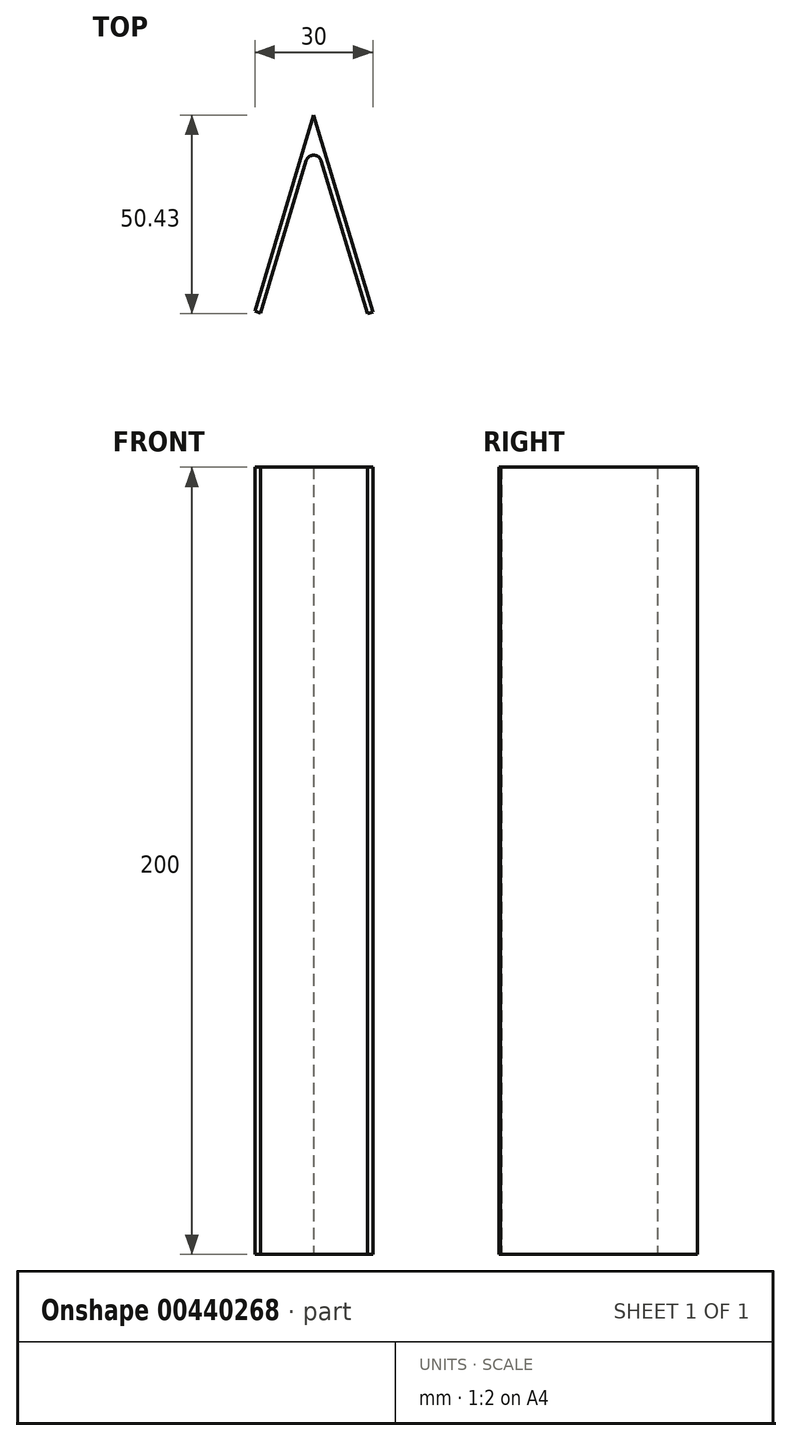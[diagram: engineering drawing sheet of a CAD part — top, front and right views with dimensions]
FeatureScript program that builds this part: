
annotation { "Feature Type Name" : "Feature", "Feature Type Description" : "" }
export const myFeature = defineFeature(function(context is Context, id is Id, definition is map)
    precondition{}
    {
        {
            var Q0;
            Q0=qCreatedBy(makeId("Top.planeOp"),FACE);
            var sketch = newSketch(context, id + "F0", { "sketchPlane" : qUnion([Q0])});
            skLineSegment(sketch, "E0", {"start": v(-0.06, 41.15) * mm, "end": v(-15, -8.66) * mm});
            skLineSegment(sketch, "E1", {"start": v(-0.06, 41.15) * mm, "end": v(15, -8.85) * mm});
            skLineSegment(sketch, "E2.0", {"start": v(1.86, 29.56) * mm, "end": v(13.56, -9.28) * mm});
            skLineSegment(sketch, "E3.0", {"start": v(-1.97, 29.56) * mm, "end": v(-13.56, -9.1) * mm});
            skArc(sketch, "E4.filletArc", {"start": v(1.86, 29.56) * mm, "mid": v(-0.05, 30.99) * mm, "end": v(-1.97, 29.56) * mm});
            skLineSegment(sketch, "E5", {"start": v(-15, -8.66) * mm, "end": v(-13.56, -9.1) * mm});
            skLineSegment(sketch, "E6", {"start": v(13.56, -9.28) * mm, "end": v(15, -8.85) * mm});
            skSolve(sketch);
        }
        {
            var Q0;
            Q0=makeQuery(id+"F0.imprint","IMPRINT",FACE,{"disambiguationData":[TD([[makeQuery(id+"F0.imprint","IMPRINT",EDGE,{"derivedFrom":sQuery(id+"F0.wireOp",EDGE,"E0")}),1.0]])]});
            extrude(context, id + "F1", {"entities" : qUnion([Q0]), "endBound" : BoundingType.SYMMETRIC, "depth" : 200 * mm, "offsetDistance" : 25 * mm});
        }
    });
